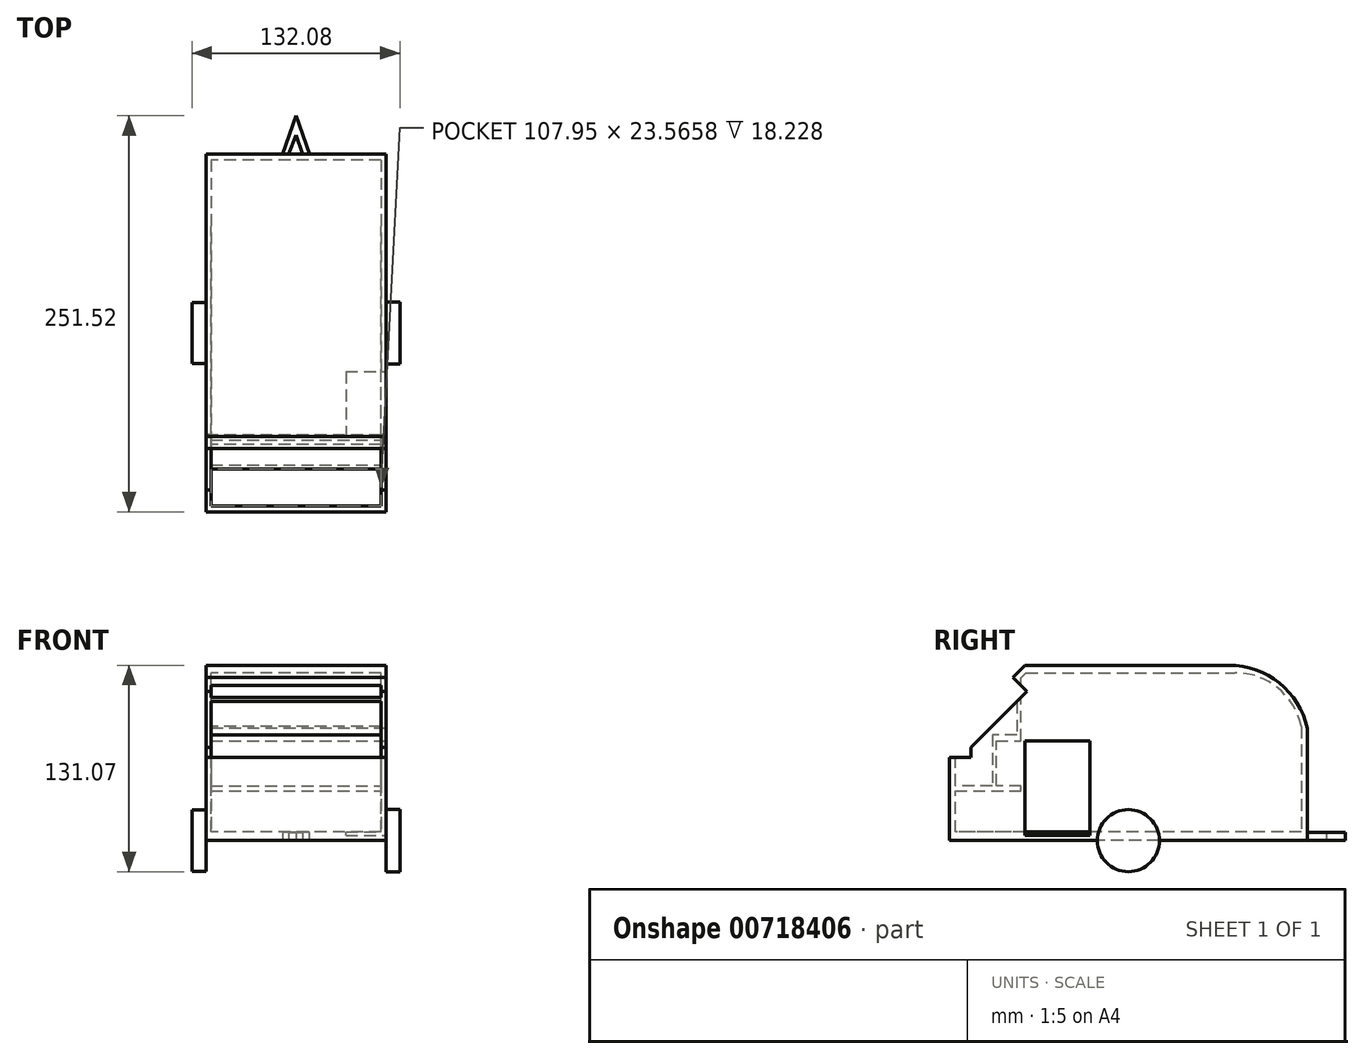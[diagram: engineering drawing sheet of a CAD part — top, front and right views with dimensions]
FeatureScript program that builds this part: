
annotation { "Feature Type Name" : "Feature", "Feature Type Description" : "" }
export const myFeature = defineFeature(function(context is Context, id is Id, definition is map)
    precondition{}
    {
        {
            var Q0;
            Q0=qCreatedBy(makeId("Right.planeOp"),FACE);
            var sketch = newSketch(context, id + "F0", { "sketchPlane" : qUnion([Q0])});
            skLineSegment(sketch, "E0", {"start": v(-92.75, -46.5) * mm, "end": v(-92.75, 16.94) * mm});
            skLineSegment(sketch, "E1", {"start": v(-92.75, 16.94) * mm, "end": v(-44.85, 64.85) * mm});
            skLineSegment(sketch, "E2", {"start": v(-44.85, 64.85) * mm, "end": v(84.85, 64.85) * mm});
            skArc(sketch, "E3", {"start": v(134.54, 24.84) * mm, "mid": v(116.75, 53.6) * mm, "end": v(84.85, 64.85) * mm});
            skLineSegment(sketch, "E4", {"start": v(134.54, 24.84) * mm, "end": v(134.54, -46.5) * mm});
            skLineSegment(sketch, "E5", {"start": v(134.54, -46.5) * mm, "end": v(-92.75, -46.5) * mm});
            skSolve(sketch);
        }
        {
            var Q0;
            Q0=makeQuery(id+"F0.imprint","IMPRINT",FACE,{"disambiguationData":[TD([[makeQuery(id+"F0.imprint","IMPRINT",EDGE,{"derivedFrom":sQuery(id+"F0.wireOp",EDGE,"E0")}),-1.0]])]});
            extrude(context, id + "F1", {"entities" : qUnion([Q0]), "endBound" : BoundingType.SYMMETRIC, "depth" : 114.3 * mm, "offsetDistance" : 25.4 * mm});
        }
        {
            var Q0;
            Q0=makeQuery(id+"F1.opExtrude","SWEPT_FACE",FACE,{"disambiguationData":[OSD([sQuery(id+"F0.wireOp",EDGE,"E5")])]});
            var sketch = newSketch(context, id + "F2", { "sketchPlane" : qUnion([Q0])});
            skLineSegment(sketch, "E6", {"start": v(0, -134.54) * mm, "end": v(57.15, -20.9) * mm});
            skLineSegment(sketch, "E7", {"start": v(57.15, -20.9) * mm, "end": v(-57.15, -20.9) * mm});
            skLineSegment(sketch, "E8", {"start": v(-57.15, -20.9) * mm, "end": v(0, -134.54) * mm});
            skLineSegment(sketch, "E9", {"start": v(28.58, -77.72) * mm, "end": v(0, -158.77) * mm});
            skLineSegment(sketch, "E10", {"start": v(0, -158.77) * mm, "end": v(-28.57, -77.72) * mm});
            skSolve(sketch);
        }
        {
            var Q0;
            {var subQ1=sQuery(id+"F2.wireOp",EDGE,"E7");Q0=makeQuery(id+"F2.imprint","IMPRINT",FACE,{"disambiguationData":[TD([[makeQuery(id+"F2.imprint","IMPRINT",EDGE,{"derivedFrom":subQ1}),1.0]])]});}
            var Q1;
            {var subQ0=sQuery(id+"F2.wireOp",EDGE,"E6");var subQ3=sQuery(id+"F2.wireOp",EDGE,"E9");var subQ4=makeQuery(id+"F2.imprint","INTERSECT",VERTEX,{"derivedFrom":[subQ0,subQ3]});Q1=makeQuery(id+"F2.imprint","IMPRINT",FACE,{"disambiguationData":[TD([[makeQuery(id+"F2.imprint","IMPRINT",EDGE,{"disambiguationData":[TD([[subQ4,-1.0]])],"derivedFrom":subQ3}),-1.0]])]});}
            var Q2;
            {var subQ0=sQuery(id+"F2.wireOp",EDGE,"E8");var subQ3=sQuery(id+"F2.wireOp",EDGE,"E10");var subQ4=makeQuery(id+"F2.imprint","INTERSECT",VERTEX,{"derivedFrom":[subQ0,subQ3]});Q2=makeQuery(id+"F2.imprint","IMPRINT",FACE,{"disambiguationData":[TD([[makeQuery(id+"F2.imprint","IMPRINT",EDGE,{"disambiguationData":[TD([[subQ4,1.0]])],"derivedFrom":subQ3}),-1.0]])]});}
            var Q3;
            {var subQ0=sQuery(id+"F2.wireOp",EDGE,"E10");var subQ1=sQuery(id+"F2.wireOp",EDGE,"E9");var subQ2=makeQuery(id+"F2.imprint","INTERSECT",VERTEX,{"derivedFrom":[subQ1,subQ0]});Q3=makeQuery(id+"F2.imprint","IMPRINT",FACE,{"disambiguationData":[TD([[makeQuery(id+"F2.imprint","IMPRINT",EDGE,{"disambiguationData":[TD([[subQ2,1.0]])],"derivedFrom":subQ1}),-1.0]])]});}
            extrude(context, id + "F3", {"entities" : qUnion([Q0, Q1, Q2, Q3]), "operationType" : NewBodyOperationType.ADD, "oppositeDirection" : true, "depth" : 5.08 * mm, "offsetDistance" : 25.4 * mm});
        }
        {
            var Q0;
            Q0=makeQuery(id+"F3.boolean.opBoolean","MERGE",FACE,{"derivedFrom":[makeQuery(id+"F1.opExtrude","SWEPT_FACE",FACE,{"disambiguationData":[OSD([sQuery(id+"F0.wireOp",EDGE,"E5")])]}),makeQuery(id+"F3.opExtrude","CAP_FACE",FACE,{"disambiguationData":[OSD([sQuery(id+"F2.wireOp",EDGE,"E6"),sQuery(id+"F2.wireOp",EDGE,"E7"),sQuery(id+"F2.wireOp",EDGE,"E8"),sQuery(id+"F2.wireOp",EDGE,"E9"),sQuery(id+"F2.wireOp",EDGE,"E10")])],"isStart":true})]});
            var sketch = newSketch(context, id + "F4", { "sketchPlane" : qUnion([Q0])});
            skLineSegment(sketch, "E11", {"start": v(0, -146.66) * mm, "end": v(4.27, -134.54) * mm});
            skPoint(sketch, "E11.startSnap0", {"position": v(4.27, -146.66) * mm});
            skLineSegment(sketch, "E12", {"start": v(4.27, -134.54) * mm, "end": v(-4.67, -134.54) * mm});
            skLineSegment(sketch, "E13", {"start": v(-4.67, -134.54) * mm, "end": v(0, -146.66) * mm});
            skSolve(sketch);
        }
        {
            var Q0;
            Q0=makeQuery(id+"F4.imprint","IMPRINT",FACE,{"disambiguationData":[TD([[makeQuery(id+"F4.imprint","IMPRINT",EDGE,{"derivedFrom":sQuery(id+"F4.wireOp",EDGE,"E11")}),1.0]])]});
            extrude(context, id + "F5", {"entities" : qUnion([Q0]), "operationType" : NewBodyOperationType.REMOVE, "oppositeDirection" : true, "depth" : 41.4 * mm, "offsetDistance" : 25.4 * mm});
        }
        {
            var Q0;
            Q0=qCreatedBy(makeId("Right.planeOp"),FACE);
            var sketch = newSketch(context, id + "F6", { "sketchPlane" : qUnion([Q0])});
            skLineSegment(sketch, "E14", {"start": v(-89.03, -41.06) * mm, "end": v(-89.03, 15.18) * mm});
            skLineSegment(sketch, "E15", {"start": v(-89.03, 15.18) * mm, "end": v(-44.04, 60.17) * mm});
            skLineSegment(sketch, "E16", {"start": v(-44.04, 60.17) * mm, "end": v(88.59, 60.17) * mm});
            skArc(sketch, "E17", {"start": v(130.77, 25.96) * mm, "mid": v(115.74, 50.54) * mm, "end": v(88.59, 60.17) * mm});
            skLineSegment(sketch, "E18", {"start": v(130.77, 25.96) * mm, "end": v(130.77, -41.06) * mm});
            skLineSegment(sketch, "E19", {"start": v(130.77, -41.06) * mm, "end": v(-89.03, -41.06) * mm});
            skSolve(sketch);
        }
        {
            var Q0;
            Q0 = qSketchRegion(id + "F6", true);
            extrude(context, id + "F7", {"entities" : qUnion([Q0]), "operationType" : NewBodyOperationType.REMOVE, "endBound" : BoundingType.SYMMETRIC, "depth" : 107.95 * mm, "offsetDistance" : 25.4 * mm});
        }
        {
            var Q0;
            Q0=makeQuery(id+"F1.opExtrude","CAP_FACE",FACE,{"disambiguationData":[OSD([sQuery(id+"F0.wireOp",EDGE,"E0"),sQuery(id+"F0.wireOp",EDGE,"E1"),sQuery(id+"F0.wireOp",EDGE,"E2"),sQuery(id+"F0.wireOp",EDGE,"E3"),sQuery(id+"F0.wireOp",EDGE,"E4"),sQuery(id+"F0.wireOp",EDGE,"E5")])],"isStart":false});
            var sketch = newSketch(context, id + "F8", { "sketchPlane" : qUnion([Q0])});
            skLineSegment(sketch, "E20.bottom", {"start": v(-44.85, -43.24) * mm, "end": v(-3.65, -43.24) * mm});
            skLineSegment(sketch, "E20.top", {"start": v(-44.85, 16.94) * mm, "end": v(-3.65, 16.94) * mm});
            skLineSegment(sketch, "E20.left", {"start": v(-44.85, -43.24) * mm, "end": v(-44.85, 16.94) * mm});
            skLineSegment(sketch, "E20.right", {"start": v(-3.65, -43.24) * mm, "end": v(-3.65, 16.94) * mm});
            skSolve(sketch);
        }
        {
            var Q0;
            Q0=makeQuery(id+"F8.imprint","IMPRINT",FACE,{"disambiguationData":[TD([[makeQuery(id+"F8.imprint","IMPRINT",EDGE,{"derivedFrom":sQuery(id+"F8.wireOp",EDGE,"E20.bottom")}),1.0]])]});
            extrude(context, id + "F9", {"entities" : qUnion([Q0]), "operationType" : NewBodyOperationType.REMOVE, "endBound" : BoundingType.SYMMETRIC, "oppositeDirection" : true, "depth" : 50.8 * mm, "offsetDistance" : 25.4 * mm});
        }
        {
            var Q0;
            Q0=makeQuery(id+"F1.opExtrude","CAP_FACE",FACE,{"disambiguationData":[OSD([sQuery(id+"F0.wireOp",EDGE,"E0"),sQuery(id+"F0.wireOp",EDGE,"E1"),sQuery(id+"F0.wireOp",EDGE,"E2"),sQuery(id+"F0.wireOp",EDGE,"E3"),sQuery(id+"F0.wireOp",EDGE,"E4"),sQuery(id+"F0.wireOp",EDGE,"E5")])],"isStart":false});
            var sketch = newSketch(context, id + "F10", { "sketchPlane" : qUnion([Q0])});
            skLineSegment(sketch, "E21", {"start": v(-92.75, -14.78) * mm, "end": v(-47.28, -14.78) * mm});
            skLineSegment(sketch, "E22", {"start": v(-47.28, -14.78) * mm, "end": v(-47.28, -11.73) * mm});
            skLineSegment(sketch, "E23", {"start": v(-47.28, -11.73) * mm, "end": v(-63.04, -11.73) * mm});
            skLineSegment(sketch, "E24", {"start": v(-63.04, -11.73) * mm, "end": v(-63.04, 16.94) * mm});
            skLineSegment(sketch, "E25", {"start": v(-63.04, 16.94) * mm, "end": v(-47.28, 16.94) * mm});
            skLineSegment(sketch, "E26", {"start": v(-47.28, 16.94) * mm, "end": v(-47.28, 62.41) * mm});
            skLineSegment(sketch, "E27", {"start": v(-47.28, 62.41) * mm, "end": v(-49.96, 59.73) * mm});
            skLineSegment(sketch, "E28", {"start": v(-49.96, 59.73) * mm, "end": v(-49.96, 20.7) * mm});
            skLineSegment(sketch, "E29", {"start": v(-49.96, 20.7) * mm, "end": v(-65.46, 20.7) * mm});
            skLineSegment(sketch, "E30", {"start": v(-65.46, 20.7) * mm, "end": v(-65.46, -11.73) * mm});
            skLineSegment(sketch, "E31", {"start": v(-65.46, -11.73) * mm, "end": v(-92.75, -11.73) * mm});
            skLineSegment(sketch, "E32", {"start": v(-92.75, -11.73) * mm, "end": v(-92.75, -14.78) * mm});
            skSolve(sketch);
        }
        {
            var Q0;
            Q0=makeQuery(id+"F10.imprint","IMPRINT",FACE,{"disambiguationData":[TD([[makeQuery(id+"F10.imprint","IMPRINT",EDGE,{"derivedFrom":sQuery(id+"F10.wireOp",EDGE,"E21")}),1.0]])]});
            extrude(context, id + "F11", {"entities" : qUnion([Q0]), "operationType" : NewBodyOperationType.ADD, "oppositeDirection" : true, "depth" : 114.3 * mm, "offsetDistance" : 25.4 * mm});
        }
        {
            var Q0;
            Q0=makeQuery(id+"F1.opExtrude","SWEPT_FACE",FACE,{"disambiguationData":[OSD([sQuery(id+"F0.wireOp",EDGE,"E1")])]});
            var sketch = newSketch(context, id + "F12", { "sketchPlane" : qUnion([Q0])});
            skLineSegment(sketch, "E33", {"start": v(57.15, 3.37) * mm, "end": v(-57.15, 3.37) * mm});
            skLineSegment(sketch, "E34", {"start": v(-57.15, 3.37) * mm, "end": v(-57.15, -53.6) * mm});
            skLineSegment(sketch, "E35", {"start": v(-57.15, -53.6) * mm, "end": v(57.15, -53.6) * mm});
            skLineSegment(sketch, "E36", {"start": v(57.15, -53.6) * mm, "end": v(57.15, 3.37) * mm});
            skSolve(sketch);
        }
        {
            var Q0;
            Q0=makeQuery(id+"F12.imprint","IMPRINT",FACE,{"disambiguationData":[TD([[makeQuery(id+"F12.imprint","IMPRINT",EDGE,{"derivedFrom":sQuery(id+"F12.wireOp",EDGE,"E33")}),1.0]])]});
            extrude(context, id + "F13", {"entities" : qUnion([Q0]), "operationType" : NewBodyOperationType.REMOVE, "oppositeDirection" : true, "depth" : 12.7 * mm, "offsetDistance" : 25.4 * mm});
        }
        {
            var Q0;
            Q0=makeQuery(id+"F1.opExtrude","CAP_FACE",FACE,{"disambiguationData":[OSD([sQuery(id+"F0.wireOp",EDGE,"E0"),sQuery(id+"F0.wireOp",EDGE,"E1"),sQuery(id+"F0.wireOp",EDGE,"E2"),sQuery(id+"F0.wireOp",EDGE,"E3"),sQuery(id+"F0.wireOp",EDGE,"E4"),sQuery(id+"F0.wireOp",EDGE,"E5")])],"isStart":false});
            var sketch = newSketch(context, id + "F14", { "sketchPlane" : qUnion([Q0])});
            skLineSegment(sketch, "E37", {"start": v(-92.75, 6.5) * mm, "end": v(-78.98, 6.5) * mm});
            skLineSegment(sketch, "E38", {"start": v(-78.98, 6.5) * mm, "end": v(-78.98, 16.94) * mm});
            skLineSegment(sketch, "E39", {"start": v(-78.98, 16.94) * mm, "end": v(-92.75, 16.94) * mm});
            skLineSegment(sketch, "E40", {"start": v(-92.75, 16.94) * mm, "end": v(-92.75, 6.5) * mm});
            skSolve(sketch);
        }
        {
            var Q0;
            {var subQ3=sQuery(id+"F14.wireOp",EDGE,"E37");Q0=makeQuery(id+"F14.imprint","IMPRINT",FACE,{"disambiguationData":[TD([[makeQuery(id+"F14.imprint","IMPRINT",EDGE,{"derivedFrom":subQ3}),1.0]])]});}
            extrude(context, id + "F15", {"entities" : qUnion([Q0]), "operationType" : NewBodyOperationType.REMOVE, "oppositeDirection" : true, "depth" : 114.3 * mm, "offsetDistance" : 25.4 * mm});
        }
        {
            var Q0;
            Q0=makeQuery(id+"F1.opExtrude","CAP_FACE",FACE,{"disambiguationData":[OSD([sQuery(id+"F0.wireOp",EDGE,"E0"),sQuery(id+"F0.wireOp",EDGE,"E1"),sQuery(id+"F0.wireOp",EDGE,"E2"),sQuery(id+"F0.wireOp",EDGE,"E3"),sQuery(id+"F0.wireOp",EDGE,"E4"),sQuery(id+"F0.wireOp",EDGE,"E5")])],"isStart":false});
            var sketch = newSketch(context, id + "F16", { "sketchPlane" : qUnion([Q0])});
            skCircle(sketch, "E41", {"center": v(20.9, -46.5) * mm, "radius": 19.72 * mm});
            skSolve(sketch);
        }
        {
            var Q0;
            {var subQ0=sQuery(id+"F16.wireOp",EDGE,"E41");var subQ1=makeQuery(id+"F1.opExtrude","CAP_EDGE",EDGE,{"disambiguationData":[OSD([sQuery(id+"F0.wireOp",EDGE,"E5")])],"isStart":false});var subQ2=makeQuery(id+"F16.imprint","INTERSECT",VERTEX,{"disambiguationData":[OD(0.0)],"derivedFrom":[subQ1,subQ0]});Q0=makeQuery(id+"F16.imprint","IMPRINT",FACE,{"disambiguationData":[TD([[makeQuery(id+"F16.imprint","IMPRINT",EDGE,{"disambiguationData":[TD([[subQ2,-1.0]])],"derivedFrom":subQ0}),1.0]])]});}
            var Q1;
            {var subQ0=sQuery(id+"F16.wireOp",EDGE,"E41");var subQ1=makeQuery(id+"F1.opExtrude","CAP_EDGE",EDGE,{"disambiguationData":[OSD([sQuery(id+"F0.wireOp",EDGE,"E5")])],"isStart":false});var subQ2=makeQuery(id+"F16.imprint","INTERSECT",VERTEX,{"disambiguationData":[OD(0.0)],"derivedFrom":[subQ1,subQ0]});Q1=makeQuery(id+"F16.imprint","IMPRINT",FACE,{"disambiguationData":[TD([[makeQuery(id+"F16.imprint","IMPRINT",EDGE,{"disambiguationData":[TD([[subQ2,1.0]])],"derivedFrom":subQ0}),1.0]])]});}
            extrude(context, id + "F17", {"entities" : qUnion([Q0, Q1]), "operationType" : NewBodyOperationType.ADD, "depth" : 8.9 * mm, "offsetDistance" : 25.4 * mm});
        }
        {
            var Q0;
            Q0=makeQuery(id+"F1.opExtrude","CAP_FACE",FACE,{"disambiguationData":[OSD([sQuery(id+"F0.wireOp",EDGE,"E0"),sQuery(id+"F0.wireOp",EDGE,"E1"),sQuery(id+"F0.wireOp",EDGE,"E2"),sQuery(id+"F0.wireOp",EDGE,"E3"),sQuery(id+"F0.wireOp",EDGE,"E4"),sQuery(id+"F0.wireOp",EDGE,"E5")])],"isStart":true});
            var sketch = newSketch(context, id + "F18", { "sketchPlane" : qUnion([Q0])});
            skCircle(sketch, "E42", {"center": v(-20.9, -46.5) * mm, "radius": 19.4 * mm});
            skSolve(sketch);
        }
        {
            var Q0;
            Q0 = qSketchRegion(id + "F18", true);
            extrude(context, id + "F19", {"entities" : qUnion([Q0]), "operationType" : NewBodyOperationType.ADD, "depth" : 8.9 * mm, "offsetDistance" : 25.4 * mm});
        }
    });
